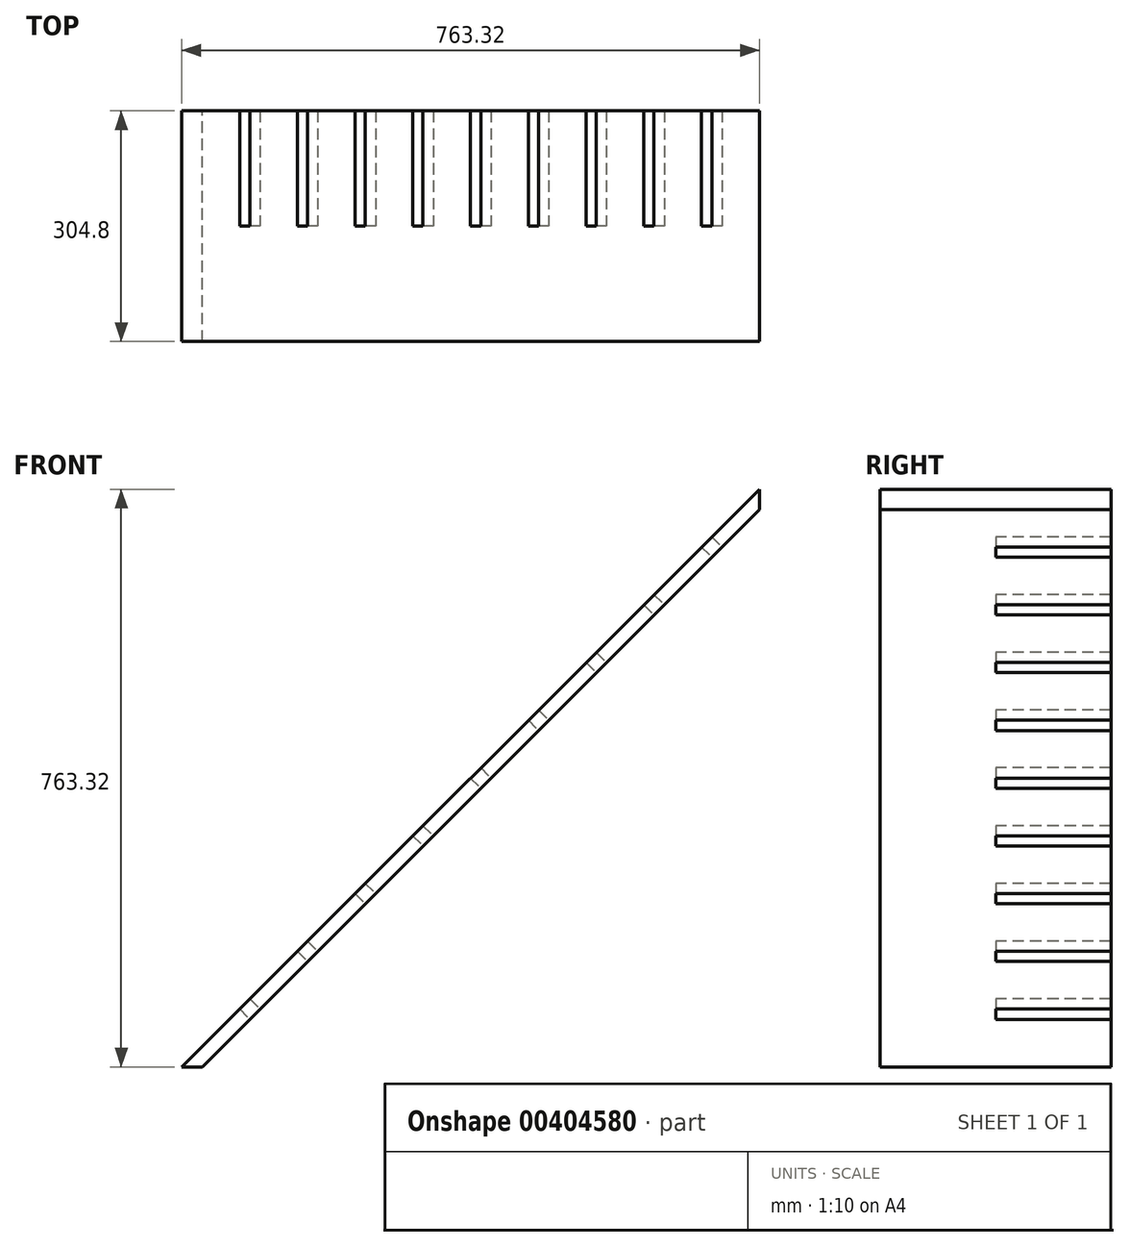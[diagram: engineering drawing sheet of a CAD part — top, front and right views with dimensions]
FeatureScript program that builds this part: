
annotation { "Feature Type Name" : "Feature", "Feature Type Description" : "" }
export const myFeature = defineFeature(function(context is Context, id is Id, definition is map)
    precondition{}
    {
        {
            var Q0;
            Q0=qCreatedBy(makeId("Front.planeOp"),FACE);
            var sketch = newSketch(context, id + "F0", { "sketchPlane" : qUnion([Q0])});
            skLineSegment(sketch, "E0", {"start": v(-421.52, 0) * mm, "end": v(341.8, 763.32) * mm});
            skPoint(sketch, "E1.MirrorP", {"position": v(67.41, 444.5) * mm});
            skLineSegment(sketch, "E2.MirrorCS", {"start": v(341.8, 763.32) * mm, "end": v(341.8, 736.38) * mm});
            skLineSegment(sketch, "E3.MirrorCS", {"start": v(-394.58, 0) * mm, "end": v(341.8, 736.38) * mm});
            skLineSegment(sketch, "E4.MirrorCS", {"start": v(-421.52, 0) * mm, "end": v(-394.58, 0) * mm});
            skSolve(sketch);
        }
        {
            var Q0;
            Q0=qSketchRegion(id+"F0",true);
            extrude(context, id + "F1", {"entities" : qUnion([Q0]), "endBound" : BoundingType.SYMMETRIC, "depth" : 304.8 * mm});
        }
        {
            var Q0;
            Q0=makeQuery(id+"F1.opExtrude","SWEPT_FACE",FACE,{"disambiguationData":[OSD([sQuery(id+"F0.wireOp",EDGE,"E3.MirrorCS")])]});
            var sketch = newSketch(context, id + "F2", { "sketchPlane" : qUnion([Q0])});
            skLineSegment(sketch, "E5.bottom", {"start": v(152.4, 692.54) * mm, "end": v(0, 692.54) * mm});
            skLineSegment(sketch, "E5.top", {"start": v(152.4, 673.49) * mm, "end": v(0, 673.49) * mm});
            skLineSegment(sketch, "E5.left", {"start": v(152.4, 692.54) * mm, "end": v(152.4, 673.49) * mm});
            skLineSegment(sketch, "E5.right", {"start": v(0, 692.54) * mm, "end": v(0, 673.49) * mm});
            skLineSegment(sketch, "E6.bottom", {"start": v(152.4, 584.59) * mm, "end": v(0, 584.59) * mm});
            skLineSegment(sketch, "E6.top", {"start": v(152.4, 565.54) * mm, "end": v(0, 565.54) * mm});
            skLineSegment(sketch, "E6.left", {"start": v(152.4, 584.59) * mm, "end": v(152.4, 565.54) * mm});
            skLineSegment(sketch, "E6.right", {"start": v(0, 584.59) * mm, "end": v(0, 565.54) * mm});
            skLineSegment(sketch, "E7.bottom", {"start": v(152.4, 476.64) * mm, "end": v(0, 476.64) * mm});
            skLineSegment(sketch, "E7.top", {"start": v(152.4, 457.59) * mm, "end": v(0, 457.59) * mm});
            skLineSegment(sketch, "E7.left", {"start": v(152.4, 476.64) * mm, "end": v(152.4, 457.59) * mm});
            skLineSegment(sketch, "E7.right", {"start": v(0, 476.64) * mm, "end": v(0, 457.59) * mm});
            skLineSegment(sketch, "E8.bottom", {"start": v(152.4, 368.69) * mm, "end": v(0, 368.69) * mm});
            skLineSegment(sketch, "E8.top", {"start": v(152.4, 349.64) * mm, "end": v(0, 349.64) * mm});
            skLineSegment(sketch, "E8.left", {"start": v(152.4, 368.69) * mm, "end": v(152.4, 349.64) * mm});
            skLineSegment(sketch, "E8.right", {"start": v(0, 368.69) * mm, "end": v(0, 349.64) * mm});
            skLineSegment(sketch, "E9.bottom", {"start": v(152.4, 260.74) * mm, "end": v(0, 260.74) * mm});
            skLineSegment(sketch, "E9.top", {"start": v(152.4, 241.69) * mm, "end": v(0, 241.69) * mm});
            skLineSegment(sketch, "E9.left", {"start": v(152.4, 260.74) * mm, "end": v(152.4, 241.69) * mm});
            skLineSegment(sketch, "E9.right", {"start": v(0, 260.74) * mm, "end": v(0, 241.69) * mm});
            skLineSegment(sketch, "E10.bottom", {"start": v(152.4, 152.79) * mm, "end": v(0, 152.79) * mm});
            skLineSegment(sketch, "E10.top", {"start": v(152.4, 133.74) * mm, "end": v(0, 133.74) * mm});
            skLineSegment(sketch, "E10.left", {"start": v(152.4, 152.79) * mm, "end": v(152.4, 133.74) * mm});
            skLineSegment(sketch, "E10.right", {"start": v(0, 152.79) * mm, "end": v(0, 133.74) * mm});
            skLineSegment(sketch, "E11.bottom", {"start": v(152.4, 44.84) * mm, "end": v(0, 44.84) * mm});
            skLineSegment(sketch, "E11.top", {"start": v(152.4, 25.79) * mm, "end": v(0, 25.79) * mm});
            skLineSegment(sketch, "E11.left", {"start": v(152.4, 44.84) * mm, "end": v(152.4, 25.79) * mm});
            skLineSegment(sketch, "E11.right", {"start": v(0, 44.84) * mm, "end": v(0, 25.79) * mm});
            skLineSegment(sketch, "E12.bottom", {"start": v(152.4, -63.11) * mm, "end": v(0, -63.11) * mm});
            skLineSegment(sketch, "E12.top", {"start": v(152.4, -82.16) * mm, "end": v(0, -82.16) * mm});
            skLineSegment(sketch, "E12.left", {"start": v(152.4, -63.11) * mm, "end": v(152.4, -82.16) * mm});
            skLineSegment(sketch, "E12.right", {"start": v(0, -63.11) * mm, "end": v(0, -82.16) * mm});
            skLineSegment(sketch, "E13.bottom", {"start": v(152.4, -171.06) * mm, "end": v(0, -171.06) * mm});
            skLineSegment(sketch, "E13.top", {"start": v(152.4, -190.11) * mm, "end": v(0, -190.11) * mm});
            skLineSegment(sketch, "E13.left", {"start": v(152.4, -171.06) * mm, "end": v(152.4, -190.11) * mm});
            skLineSegment(sketch, "E13.right", {"start": v(0, -171.06) * mm, "end": v(0, -190.11) * mm});
            skSolve(sketch);
        }
        {
            var Q0;
            Q0=qSketchRegion(id+"F2",true);
            extrude(context, id + "F3", {"entities" : qUnion([Q0]), "operationType" : NewBodyOperationType.REMOVE, "oppositeDirection" : true, "depth" : 19.05 * mm});
        }
    });
